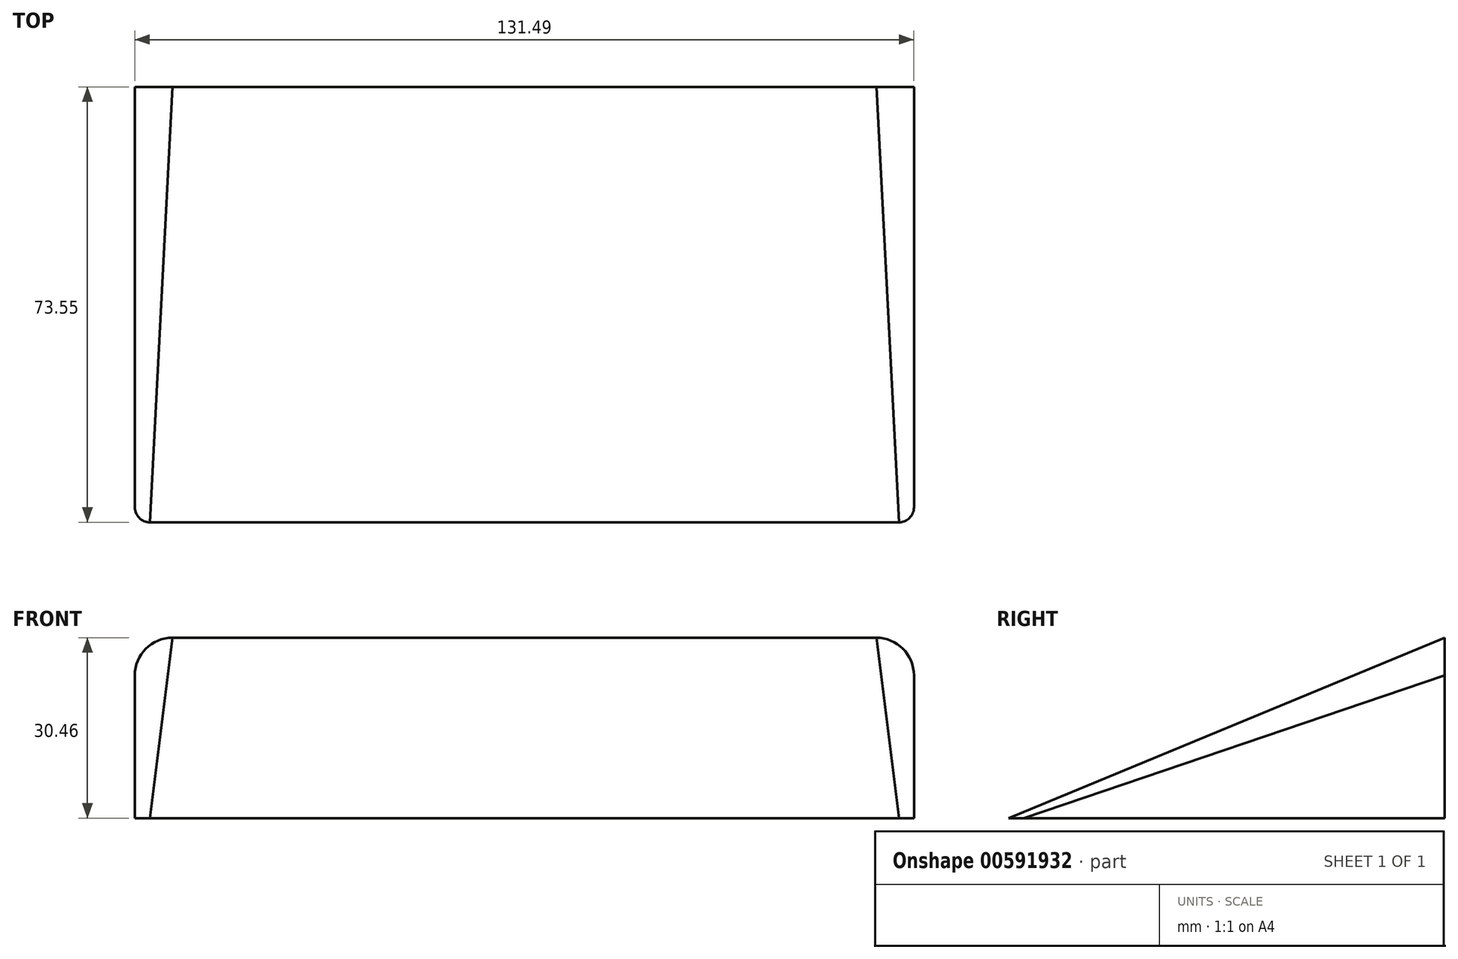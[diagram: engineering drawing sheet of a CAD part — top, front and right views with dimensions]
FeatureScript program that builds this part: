
annotation { "Feature Type Name" : "Feature", "Feature Type Description" : "" }
export const myFeature = defineFeature(function(context is Context, id is Id, definition is map)
    precondition{}
    {
        {
            var Q0;
            Q0=qCreatedBy(makeId("Front.planeOp"),FACE);
            var sketch = newSketch(context, id + "F0", { "sketchPlane" : qUnion([Q0])});
            skLineSegment(sketch, "E0.bottom", {"start": v(-56.13, 30.46) * mm, "end": v(62.66, 30.46) * mm});
            skLineSegment(sketch, "E0.top", {"start": v(-62.48, 0) * mm, "end": v(69.01, 0) * mm});
            skLineSegment(sketch, "E0.left", {"start": v(-62.48, 24.1) * mm, "end": v(-62.48, 0) * mm});
            skLineSegment(sketch, "E0.right", {"start": v(69.01, 24.1) * mm, "end": v(69.01, 0) * mm});
            skPoint(sketch, "E1.visualSharp", {"position": v(-62.48, 30.46) * mm});
            skArc(sketch, "E1.filletArc", {"start": v(-56.13, 30.46) * mm, "mid": v(-60.62, 28.6) * mm, "end": v(-62.48, 24.1) * mm});
            skPoint(sketch, "E2.visualSharp", {"position": v(69.01, 30.46) * mm});
            skArc(sketch, "E2.filletArc", {"start": v(69.01, 24.1) * mm, "mid": v(67.15, 28.6) * mm, "end": v(62.66, 30.46) * mm});
            skSolve(sketch);
        }
        {
            var Q0;
            Q0=qCreatedBy(makeId("Top.planeOp"),FACE);
            var sketch = newSketch(context, id + "F1", { "sketchPlane" : qUnion([Q0])});
            skLineSegment(sketch, "E3.bottom", {"start": v(-62.48, 0) * mm, "end": v(69.01, 0) * mm});
            skLineSegment(sketch, "E3.top", {"start": v(-59.94, -73.55) * mm, "end": v(66.47, -73.55) * mm});
            skLineSegment(sketch, "E3.left", {"start": v(-62.48, 0) * mm, "end": v(-62.48, -71) * mm});
            skLineSegment(sketch, "E3.right", {"start": v(69.01, 0) * mm, "end": v(69.01, -71) * mm});
            skPoint(sketch, "E4.visualSharp", {"position": v(-62.48, -73.55) * mm});
            skArc(sketch, "E4.filletArc", {"start": v(-62.48, -71) * mm, "mid": v(-61.73, -72.8) * mm, "end": v(-59.94, -73.55) * mm});
            skPoint(sketch, "E5.visualSharp", {"position": v(69.01, -73.55) * mm});
            skArc(sketch, "E5.filletArc", {"start": v(66.47, -73.55) * mm, "mid": v(68.27, -72.8) * mm, "end": v(69.01, -71) * mm});
            skSolve(sketch);
        }
        {
            var Q0;
            Q0=makeQuery(id+"F0.imprint","IMPRINT",FACE,{"disambiguationData":[TD([[makeQuery(id+"F0.imprint","IMPRINT",EDGE,{"derivedFrom":sQuery(id+"F0.wireOp",EDGE,"E0.bottom")}),-1.0]])]});
            var Q1;
            Q1=makeQuery(id+"F1.imprint","IMPRINT",FACE,{"disambiguationData":[TD([[makeQuery(id+"F1.imprint","IMPRINT",EDGE,{"derivedFrom":sQuery(id+"F1.wireOp",EDGE,"E3.bottom")}),-1.0]])]});
            var Q2;
            Q2=sQuery(id+"F0.wireOp",VERTEX,"E1.filletArc.end");
            var Q3;
            Q3=sQuery(id+"F1.wireOp",VERTEX,"E4.filletArc.start");
            loft(context, id + "F2", {"sheetProfilesArray" : [{ "sheetProfileEntities" : qUnion([Q0]) }, { "sheetProfileEntities" : qUnion([Q1]) }], "matchConnections" : true, "connections" : [{ "connectionEntities" : qUnion([Q2, Q3]), "connectionEdgeQueries" : qUnion([]), "connectionEdgeParameters" : [] }]});
        }
    });
